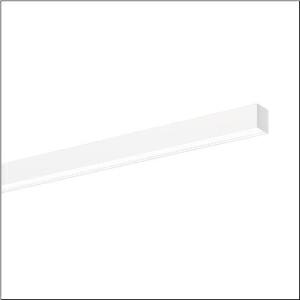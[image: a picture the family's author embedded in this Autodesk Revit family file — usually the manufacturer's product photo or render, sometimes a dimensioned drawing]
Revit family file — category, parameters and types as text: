
# Revit family: silica_r__21_51mx20dc45wb_dec1
name_source: partatom
category: Lighting Fixtures
units: mm (PartAtom-declared; Revit-internal decimal feet)

## family parameters
Cut with Voids When Loaded = No
Host = Face
Light Source = No
Part Type = Normal
Room Calculation Point = No
Round Connector Dimension = Use Diameter
Shared = No

## types (1)
- --- (1 x LED, 6000 lm, 40.1 W, 4000K)
    Apparent Load = 40 VA
    CIE Flux Codes = 48 79 96 100 100
    Color Rendering = 80
    Color Temperature = 4000K
    Default Elevation = 1800 mm
    Description = Silica® 21, office luminaire, primary optical cover: cover, of PMMA, opal, light emission: direct distribution, primary light characteristic: symmetric, installation type: surface-mounted, LED, rated luminous flux: 6.000lm, luminous efficacy: 150lm/W, light colour: 840, colour temperature: 4000K, with terminal, 3+2-pole, max. 2.5mm², mains connection: 220..240V, AC, 50/60Hz, rated input power: 40.1W, luminaire housing, of aluminium, traffic white (RAL 9016), length: 3.004mm, width: 53mm, height: 53mm, protection rating (complete): IP20, insulation class (complete): insulation class I (protective earthing), certification: CE, permissible operating ambient temperature: 0..+35°C, standard: EN 50419, packaging unit: 1 piece
    Height = 0 mm  [stored 0 ft]
    Lamp = 1 x LED
    Lamp Light Flux = 6000 lm
    Lamp Power = 40.1 W
    Lamp count = 1
    Length = 3004 mm
    Luminous efficacy = 150 lm/W
    Manufacturer = Siteco
    ModVariant = No
    Model = 51MX20DC45WB
    Mounting Place = Ceiling
    Mounting Type = Recessed
    Number of Poles = 1
    OnlyDefault = Yes
    Power Factor = 1
    Product Name = Silica® 21
    Product group = office luminaire | ceiling recessed
    ProductGroupID = 401
    Protection Class = Protection class I
    Protection Degree = IP 20
    RLX_Detail_Level = 1
    RLX_Emergency_Light_Flux = 0 lm
    RLX_Emergency_Type = 0
    RLX_Emergency_Type_DB = No
    RlxData = <blob elided: 23829 chars, md5=342692bd>
    Socket = socket
    Standby Power = 0 W
    System Light Flux = 6000 lm
    System Power = 40 W
    Type Comments = factory setting: luminous flux: 100 % | dim-lin: 254 | 218 mA
    Type Image = l_1297777.jpg
    URL = http://relux.com
    VarID = @adj_048005
    Voltage = 0 V
    Weight = 0.00 kg
    Width = 53 mm

note: [stored X ft] marks values corroborated as IEEE doubles in the binary element streams (Revit-internal decimal feet)

## geometry (parser evidence)
native form markers: Blend x4, Sweep x12
no freeform markers — native parametric forms only
